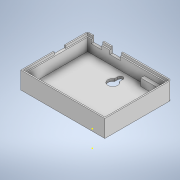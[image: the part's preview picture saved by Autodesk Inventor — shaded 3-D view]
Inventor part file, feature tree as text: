
AUTODESK INVENTOR PART (.ipt)
format: ipt  version: 2022 (Build 260153000, 153)  size: 235,008 bytes
history: native  units: in
note: dims shown in document units (in); Inventor stores cm internally (conversion verified against a paired STEP export)
features: sketch x7, extrude x7, fillet x2
ambient origin geometry x8: Origin, YZ Plane, XZ Plane, XY Plane, X Axis, Y Axis, Z Axis, Center Point
bodies: Solid1 (feature_tree)
feature tree (16):
  sketch  "Sketch1"  dims[d2=0.5512in d3=0.0in d6=0.0787in]
  extrude  "Extrusion1"  Depth=0.0787in
  sketch  "Sketch3"  dims[d8=0.0787in d13=0.4724in d14=0.0in]
  extrude  "Extrusion2"  Depth=0.4724in TaperAngle=0.0deg
  extrude  "Extrusion5"  Depth=0.5906in
  extrude  "Extrusion7"  Depth=0.2362in TaperAngle=0.0deg
  extrude  "Extrusion8"  Depth=0.0787in TaperAngle=0.0deg
  extrude  "Extrusion9"  Depth=0.0394in
  extrude  "Extrusion10"  Depth=0.0787in
  fillet  "Fillet7"  Radius=0.0787in
  fillet  "Fillet8"  Radius=0.1181in
  sketch  "Sketch4"  dims[d55=0.1181in d56=0.5906in]
  sketch  "Sketch10"  dims[d60=0.5906in d64=0.2362in d65=0.0in]
  sketch  "Sketch12"  dims[d79=0.1969in d80=0.0in d88=0.0787in d89=0.0in]
  sketch  "Sketch15"  dims[d94=0.0394in d95=0.0394in d96=0.0394in d97=0.0394in d99=0.0394in]
  sketch  "Sketch16"  dims[d101=0.0394in d102=0.0787in d104=0.0787in d108=0.1181in d118=0.315in d125=0.3937in d126=0.0in d127=0.3346in d128=0.3346in d131=1.126in d132=0.5315in d133=0.3937in d134=0.0in d140=1.0933in d141=0.3543in d143=0.1969in d144=0.0787in d145=0.0787in d148=0.1969in d149=0.2362in d150=0.1575in d151=2.6772in d152=2.126in d153=0.0787in d154=0.0787in d155=0.0in d156=1.3386in d157=0.0394in d40=0.0197in d41=0.0344in d42=0.0197in d43=0.0344in d66=0.0197in d67=0.0344in d74=0.0197in d75=0.0344in d76=0.0197in d77=0.0344in d115=0.0in d116=0.0in d117=0.0in d135=0.0197in d136=0.0344in d137=0.0197in d138=0.0344in]
